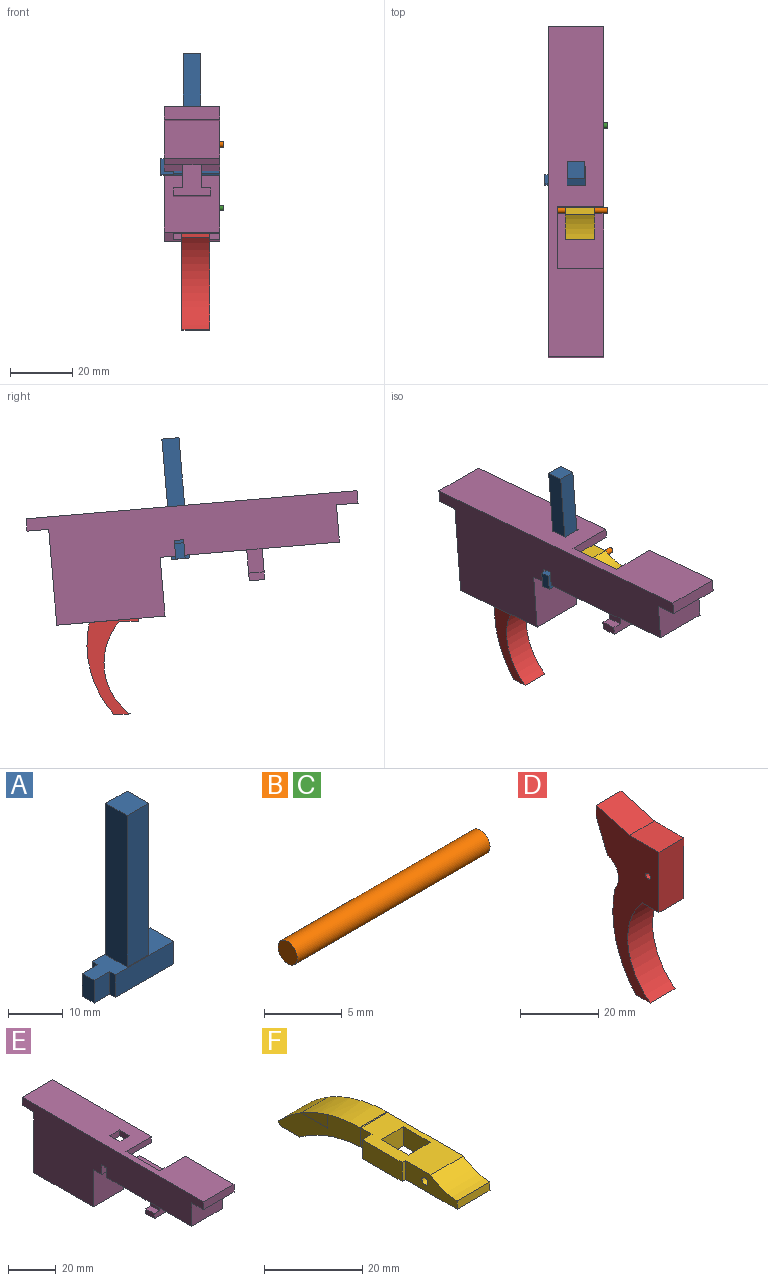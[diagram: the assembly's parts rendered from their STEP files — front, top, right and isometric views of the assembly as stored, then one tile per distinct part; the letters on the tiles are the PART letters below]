
ASSEMBLY  parts=6 mates=5
PART A: 15 faces, bbox 19x6x38.9 mm
  f0: plane 5.05x1.5mm, normal (-1,0,0), area 7.6mm2, adj f7,f10,f11,f13
  f1: plane 33.85x5.5mm, normal (0,1,0), area 186.2mm2, adj f2,f4,f5,f11
  f2: plane 33.85x5.5mm, normal (-1,0,0), area 186.2mm2, adj f1,f3,f5,f11
  f3: plane 33.85x5.5mm, normal (0,-1,0), area 186.2mm2, adj f2,f4,f5,f11
  f4: plane 33.85x5.5mm, normal (1,0,0), area 186.2mm2, adj f1,f3,f5,f11
  f5: plane 5.5x5.5mm, normal (0,0,1), area 30.2mm2, adj f1,f2,f3,f4
  f6: plane 5.05x1.5mm, normal (-1,0,0), area 7.6mm2, adj f9,f10,f11,f12
  f7: plane 15x5.05mm, normal (0,-1,0), area 75.7mm2, adj f0,f8,f10,f11
  f8: plane 6x5.05mm, normal (1,0,0), area 30.3mm2, adj f7,f9,f10,f11
  f9: plane 15x5.05mm, normal (0,1,0), area 75.7mm2, adj f6,f8,f10,f11
  f10: plane 19x6mm, normal (0,0,-1), area 102mm2, adj f0,f6,f7,f8,f9,f12,f13,f14
  f11: plane 19x6mm, normal (0,0,1), area 71.7mm2, adj f0,f1,f2,f3,f4,f6,f7,f8
  f12: plane 5.05x4mm, normal (0,1,0), area 20.2mm2, adj f6,f10,f11,f14
  f13: plane 5.05x4mm, normal (0,-1,0), area 20.2mm2, adj f0,f10,f11,f14
  f14: plane 5.05x3mm, normal (-1,0,0), area 15.2mm2, adj f10,f11,f12,f13
PART B: 3 faces, bbox 17.5x1.8x1.8 mm
  f0: cylinder r=0.88mm len=17.5mm, axis (-1,0,0), area 96.2mm2, adj f1,f2
  f1: plane 1.75x1.75mm, normal (1,0,0), area 2.4mm2, adj f0
  f2: plane 1.75x1.75mm, normal (-1,0,0), area 2.4mm2, adj f0
PART C: same geometry as B
PART D: 13 faces, bbox 9x22.7x52.1 mm
  f0: plane 10.64x9mm, normal (0,0,1), area 95.7mm2, adj f1,f9,f10,f11
  f1: plane 18.86x9mm, normal (0,-1,0), area 169.7mm2, adj f0,f2,f10,f11
  f2: plane 9x6.03mm, normal (0,0,-1), area 54.3mm2, adj f1,f3,f10,f11
  f3: cylinder r=20.29mm len=29.89mm, axis (-1,0,0), area 304.2mm2, adj f2,f4,f10,f11
  f4: plane 9x5.28mm, normal (0,0,-1), area 47.5mm2, adj f3,f5,f10,f11
  f5: cylinder r=33.77mm len=29.89mm, axis (-1,0,0), area 287.5mm2, adj f4,f6,f10,f11
  f6: cylinder r=5.47mm len=9mm, axis (-1,0,0), area 96.7mm2, adj f5,f7,f10,f11
  f7: plane 10.2x9mm, normal (0,0.93,-0.38), area 99.1mm2, adj f6,f8,f10,f11
  f8: plane 9x3.34mm, normal (0,1,0), area 30.1mm2, adj f7,f9,f10,f11
  f9: plane 12.08x9mm, normal (0,-0.27,0.96), area 112.8mm2, adj f0,f8,f10,f11
  f10: plane 52.09x22.72mm, normal (1,0,0), area 524.8mm2, adj f0,f1,f2,f3,f4,f5,f6,f7
  f11: plane 52.09x22.72mm, normal (-1,0,0), area 524.8mm2, adj f0,f1,f2,f3,f4,f5,f6,f7
  f12: cylinder r=0.88mm len=9mm, axis (1,0,0), area 49.5mm2, adj f10,f11
PART E: 64 faces, bbox 18x107x35 mm
  f0: plane 5.87x3mm, normal (0,-1,0), area 17.6mm2, adj f22,f39,f60,f62
  f1: plane 5.87x3mm, normal (0,1,0), area 17.6mm2, adj f22,f39,f60,f62
  f2: plane 37.02x32.01mm, normal (1,0,0), area 909.1mm2, adj f4,f7,f11,f36,f37,f38,f39,f46
  f3: plane 46.98x16.02mm, normal (1,0,0), area 478.9mm2, adj f6,f15,f22,f39,f40,f41,f42,f43
  f4: plane 5.01x3mm, normal (0,-1,0), area 12mm2, adj f2,f5,f7,f8,f52,f55
  f5: plane 3x1.5mm, normal (0,0,-1), area 4.5mm2, adj f4,f6,f8,f55
  f6: plane 5x3mm, normal (0,1,0), area 12mm2, adj f3,f5,f8,f15,f51,f55
  f7: plane 18x5.02mm, normal (0,0,-1), area 67.8mm2, adj f2,f4,f8,f10,f18,f46
  f8: plane 107x35.04mm, normal (-1,0,0), area 2194.6mm2, adj f4,f5,f6,f7,f11,f15,f17,f18
  f9: plane 58.31x35.02mm, normal (1,0,0), area 289.6mm2, adj f11,f19,f20,f21,f22,f36,f37,f38
  f10: plane 21.99x8.9mm, normal (1,0,0), area 83.6mm2, adj f7,f11,f18,f46,f47,f48,f49,f50
  f11: plane 35x18mm, normal (0,0,-1), area 289.2mm2, adj f2,f8,f9,f10,f18,f19,f36,f50
  f12: plane 12x10mm, normal (0,-1,0), area 75mm2, adj f13,f17,f26,f27,f28,f31,f32,f33
  f13: plane 12x5mm, normal (0,0,-1), area 60mm2, adj f12,f14,f26,f32
  f14: plane 12x10mm, normal (0,1,0), area 75mm2, adj f13,f15,f26,f27,f28,f31,f32,f33
  f15: plane 19.98x18mm, normal (0,0,-1), area 336mm2, adj f3,f6,f8,f14,f16,f28,f30,f33
  f16: plane 55.48x16.03mm, normal (1,0,0), area 268.2mm2, adj f15,f17,f22,f23,f24,f25,f34,f35
  f17: plane 25x18mm, normal (0,0,-1), area 450mm2, adj f8,f12,f16,f25,f29,f34
  f18: plane 19x18mm, normal (0,-1,0), area 342mm2, adj f7,f8,f10,f11
  f19: plane 31x18mm, normal (0,1,0), area 558mm2, adj f8,f9,f11,f20
  f20: plane 18x7mm, normal (0,0,-1), area 126mm2, adj f8,f9,f19,f21
  f21: plane 18x4mm, normal (0,1,0), area 72mm2, adj f8,f9,f20,f22
  f22: plane 107x18mm, normal (0,0,1), area 1590.7mm2, adj f0,f1,f3,f8,f9,f16,f21,f23
  f23: plane 18x4mm, normal (0,-1,0), area 72mm2, adj f8,f16,f22,f24
  f24: plane 18x7mm, normal (0,0,-1), area 126mm2, adj f8,f16,f23,f25
  f25: plane 18x12mm, normal (0,-1,0), area 216mm2, adj f8,f16,f17,f24
  f26: plane 5x2.5mm, normal (-1,0,0), area 12.5mm2, adj f12,f13,f14,f27
  f27: plane 5x3mm, normal (0,0,1), area 15mm2, adj f12,f14,f26,f28
  f28: plane 7.5x5.1mm, normal (-1,0,0), area 37.5mm2, adj f12,f14,f15,f27,f29,f30
  f29: plane 6x5.1mm, normal (0,0,-1), area 30.6mm2, adj f8,f17,f28,f30
  f30: plane 6x0mm, normal (0,-1,0), area 0mm2, adj f8,f15,f28,f29
  f31: plane 5x3mm, normal (0,0,1), area 15mm2, adj f12,f14,f32,f33
  f32: plane 5x2.5mm, normal (1,0,0), area 12.5mm2, adj f12,f13,f14,f31
  f33: plane 7.5x5.1mm, normal (1,0,0), area 37.5mm2, adj f12,f14,f15,f31,f34,f35
  f34: plane 6x5.1mm, normal (0,0,-1), area 30.6mm2, adj f16,f17,f33,f35
  f35: plane 6x0mm, normal (0,-1,0), area 0mm2, adj f15,f16,f33,f34
  f36: plane 15x3.01mm, normal (0,-1,0), area 45.1mm2, adj f2,f9,f11,f37
  f37: plane 15x3.9mm, normal (0,0,1), area 58.5mm2, adj f2,f9,f36,f38
  f38: plane 29x15mm, normal (0,-1,0), area 435mm2, adj f2,f9,f37,f39
  f39: plane 48.32x16.5mm, normal (0,0,-1), area 659.7mm2, adj f0,f1,f2,f3,f9,f38,f40,f53
  f40: plane 15x3mm, normal (0,-1,0), area 45mm2, adj f3,f9,f22,f39
  f41: plane 15x3mm, normal (0,1,0), area 45mm2, adj f3,f16,f22,f42
  f42: plane 18.69x15mm, normal (0,0,-1), area 280.3mm2, adj f3,f16,f41,f43
  f43: plane 15x10mm, normal (0,1,0), area 149.9mm2, adj f3,f16,f42,f44
  f44: plane 45.48x15mm, normal (0,0,1), area 682.2mm2, adj f3,f16,f43,f45
  f45: plane 15x2.99mm, normal (0,1,0), area 44.8mm2, adj f3,f15,f16,f44
  f46: plane 15x2.98mm, normal (0,-1,0), area 44.8mm2, adj f2,f7,f10,f47
  f47: plane 15x6.51mm, normal (0,0,1), area 97.7mm2, adj f2,f10,f46,f48
  f48: plane 18.96x15mm, normal (0,1,0), area 284.3mm2, adj f2,f10,f47,f49
  f49: plane 15x2.39mm, normal (0,0,1), area 35.8mm2, adj f2,f10,f48,f50
  f50: plane 15x3.02mm, normal (0,1,0), area 45.3mm2, adj f2,f10,f11,f49
  f51: plane 5.36x1.5mm, normal (0,0,1), area 8mm2, adj f3,f6,f54,f55
  f52: plane 8.27x1.5mm, normal (0,0,1), area 12.4mm2, adj f2,f4,f53,f55
  f53: plane 10.03x1.5mm, normal (0,-1,0), area 15.1mm2, adj f2,f39,f52,f55
  f54: plane 9.98x1.5mm, normal (0,1,0), area 15mm2, adj f3,f39,f51,f55
  f55: plane 16.63x10.04mm, normal (1,0,0), area 160.5mm2, adj f4,f5,f6,f39,f51,f52,f53,f54
  f56: cylinder r=0.88mm len=1.75mm, axis (1,0,0), area 8.3mm2, adj f3,f57
  f57: plane 1.75x1.75mm, normal (1,0,0), area 2.4mm2, adj f56
  f58: cylinder r=0.88mm len=1.75mm, axis (1,0,0), area 8.2mm2, adj f2,f59
  f59: plane 1.75x1.75mm, normal (1,0,0), area 2.4mm2, adj f58
  f60: plane 6.01x3mm, normal (1,0,0), area 18mm2, adj f0,f1,f22,f61
  f61: plane 6.01x3.24mm, normal (0,0,-1), area 19.4mm2, adj f39,f60
  f62: plane 6.01x3mm, normal (-1,0,0), area 18mm2, adj f0,f1,f22,f63
  f63: plane 6.01x5.89mm, normal (0,0,-1), area 35.4mm2, adj f9,f39,f62
PART F: 25 faces, bbox 10.4x53.2x11 mm
  f0: plane 53.24x11.01mm, normal (1,0,0), area 237.6mm2, adj f2,f5,f11,f16,f17,f18,f19,f21
  f1: plane 7.67x3.35mm, normal (-1,-0.01,0), area 14.3mm2, adj f3,f15,f23
  f2: cylinder r=32.5mm len=7.82mm, axis (1,0,0), area 1.8mm2, adj f0,f3,f16,f20,f23
  f3: plane 23.76x11mm, normal (-1,0,0), area 100.6mm2, adj f1,f2,f15,f18,f19,f20,f21,f22
  f4: plane 4.7x3.15mm, normal (-1,-0.01,0), area 14.8mm2, adj f5,f12,f16,f20
  f5: plane 29.47x10.44mm, normal (0,0,-1), area 235.1mm2, adj f0,f4,f6,f7,f8,f9,f10,f11
  f6: plane 7.77x4.7mm, normal (1,0,0), area 36.5mm2, adj f5,f7,f14,f16
  f7: plane 6.33x4.7mm, normal (0,-1,0), area 29.7mm2, adj f5,f6,f8,f16
  f8: plane 7.77x4.7mm, normal (-1,0,0), area 36.5mm2, adj f5,f7,f14,f16
  f9: plane 4.7x0.99mm, normal (0,-1,0), area 4.6mm2, adj f5,f10,f13,f16
  f10: plane 14.89x4.7mm, normal (-1,0,0), area 54.1mm2, adj f5,f9,f11,f16,f17,f24
  f11: plane 9.46x2.09mm, normal (0,-1,0), area 19.8mm2, adj f0,f5,f10,f24
  f12: plane 4.7x2.78mm, normal (-0.01,1,0), area 13.1mm2, adj f4,f5,f13,f16
  f13: plane 11.4x4.7mm, normal (-1,0,0), area 53.6mm2, adj f5,f9,f12,f16
  f14: plane 6.33x4.7mm, normal (0,1,0), area 29.7mm2, adj f5,f6,f8,f16
  f15: plane 7.67x0.1mm, normal (0,0,-1), area 0.4mm2, adj f1,f3,f23
  f16: plane 21.8x10.44mm, normal (0,0,1), area 162.5mm2, adj f0,f2,f4,f6,f7,f8,f9,f10
  f17: cylinder r=0.88mm len=9.45mm, axis (1,0,0), area 52mm2, adj f0,f10
  f18: cylinder r=32.5mm len=7.82mm, axis (1,0,0), area 67.5mm2, adj f0,f3,f19,f23
  f19: plane 7.82x0.92mm, normal (0,0.7,-0.71), area 10.1mm2, adj f0,f3,f18,f22
  f20: plane 4.7x0.12mm, normal (0,-1,0), area 0.6mm2, adj f2,f3,f4,f21
  f21: cylinder r=32.5mm len=17.54mm, axis (1,0,0), area 147.8mm2, adj f0,f3,f5,f20,f22
  f22: plane 7.82x5.3mm, normal (0,0,-1), area 41.4mm2, adj f0,f3,f19,f21
  f23: cylinder r=33.29mm len=16.83mm, axis (1,0,0), area 138.6mm2, adj f0,f1,f2,f3,f15,f18
  f24: cylinder r=13.41mm len=9.45mm, axis (1,0,0), area 77.9mm2, adj f0,f10,f11,f16
PLACE A rot(axis=(-1,0,0),4.8deg) t=(-5.14,1.94,-22.59)mm
PLACE B rot(axis=(-1,0,0),4.8deg) t=(-5.04,1.9,-23.06)mm
PLACE C rot(axis=(-1,0,0),4.8deg) t=(-5.04,29.24,-43.53)mm
PLACE D rot(axis=(-1,0,0),1.1deg) t=(-3.89,0.2,-22.37)mm
PLACE E rot(axis=(-1,0,0),4.8deg) t=(-5.14,2.02,-21.61)mm
PLACE F rot(axis=(-1,0,0),4.3deg) t=(-3.66,1.94,-21.44)mm
MATE fastened B.f0 <-> E.f56  axis (-1,0,0) through (-12.64,-14.75,-29.18)mm
MATE fastened C.f0 <-> E.f58  axis (-1,0,0) through (-12.64,12.6,-49.65)mm
MATE fastened E.f46 <-> A.f9  axis (0,-1,0.08) through (-3.64,-1.92,-36.69)mm
MATE revolute F.f17 <-> B.f0  axis (1,0,0) through (-3.89,-14.75,-29.18)mm
MATE revolute D.f12 <-> C.f0  axis (1,0,0) through (-3.89,12.6,-49.65)mm
